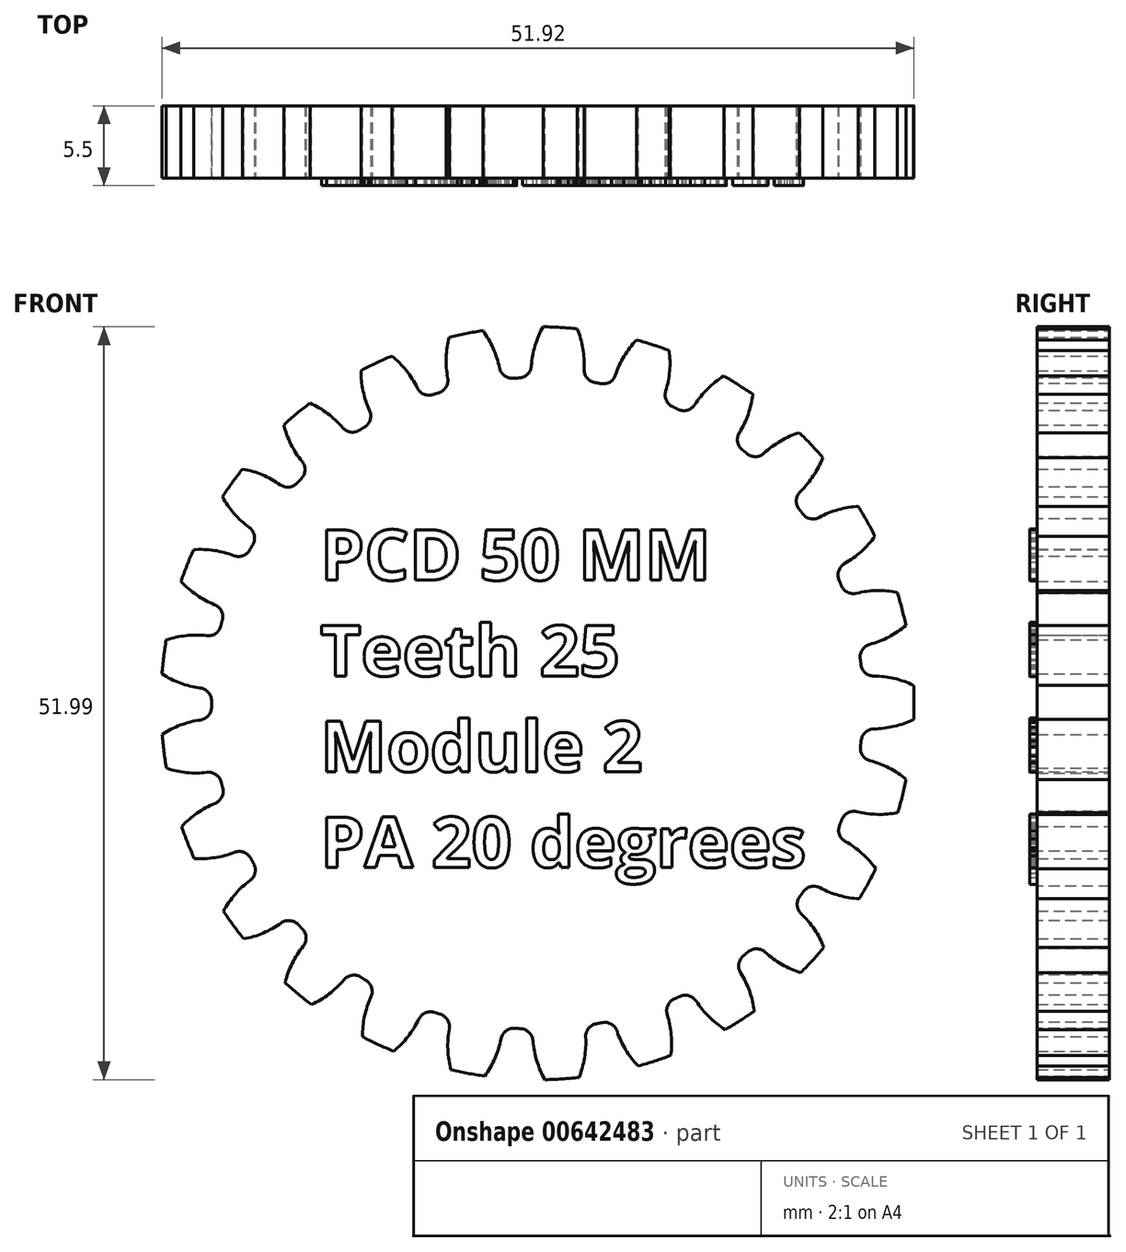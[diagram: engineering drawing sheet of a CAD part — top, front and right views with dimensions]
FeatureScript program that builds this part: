
annotation { "Feature Type Name" : "Feature", "Feature Type Description" : "" }
export const myFeature = defineFeature(function(context is Context, id is Id, definition is map)
    precondition{}
    {
        {
            var Q0;
            Q0=qCreatedBy(makeId("Front.planeOp"),FACE);
            var sketch = newSketch(context, id + "F0", { "sketchPlane" : qUnion([Q0])});
            skCircle(sketch, "E0", {"center": v(0, 0) * mm, "radius": 25 * mm, "construction": true});
            skLineSegment(sketch, "E1", {"start": v(0, 0) * mm, "end": v(0, 29.13) * mm, "construction": true});
            skLineSegment(sketch, "E2", {"start": v(0, 25) * mm, "end": v(44.14, 25) * mm, "construction": true});
            skLineSegment(sketch, "E3", {"start": v(0, 25) * mm, "end": v(44.14, 8.94) * mm});
            skLineSegment(sketch, "E4", {"start": v(0, 0) * mm, "end": v(8.03, 22.08) * mm, "construction": true});
            skCircle(sketch, "E5", {"center": v(0, 0) * mm, "radius": 23.5 * mm, "construction": true});
            skPoint(sketch, "E6", {"position": v(0, 26) * mm});
            skPoint(sketch, "E7", {"position": v(0, 23.5) * mm});
            skPoint(sketch, "E8", {"position": v(0, 25.16) * mm});
            skLineSegment(sketch, "E9", {"start": v(0, 25.16) * mm, "end": v(8.03, 22.08) * mm, "construction": true});
            skPoint(sketch, "E10", {"position": v(6.03, 22.85) * mm});
            skArc(sketch, "E11", {"start": v(0.4, 26) * mm, "mid": v(-0.26, 24.3) * mm, "end": v(-0.42, 22.5) * mm});
            skArc(sketch, "E12", {"start": v(-0.42, 22.5) * mm, "mid": v(12.32, 21.4) * mm, "end": v(0.4, 26) * mm, "construction": true});
            skPoint(sketch, "E13", {"position": v(-0.06, 25) * mm});
            skPoint(sketch, "E14", {"position": v(1.51, 24.95) * mm});
            skLineSegment(sketch, "E15", {"start": v(0, 0) * mm, "end": v(1.51, 24.95) * mm, "construction": true});
            skArc(sketch, "E16.MirrorCS", {"start": v(2.75, 25.85) * mm, "mid": v(3.2, 24.1) * mm, "end": v(3.13, 22.28) * mm});
            skArc(sketch, "E17", {"start": v(2.75, 25.85) * mm, "mid": v(1.57, 25.95) * mm, "end": v(0.4, 26) * mm});
            skArc(sketch, "E18", {"start": v(0.4, 26) * mm, "mid": v(-1.57, -25.95) * mm, "end": v(2.75, 25.85) * mm, "construction": true});
            skArc(sketch, "E19", {"start": v(-0.42, 22.5) * mm, "mid": v(-1.36, -22.46) * mm, "end": v(3.13, 22.28) * mm});
            skArc(sketch, "E20", {"start": v(3.13, 22.28) * mm, "mid": v(1.36, 22.46) * mm, "end": v(-0.42, 22.5) * mm, "construction": true});
            skSolve(sketch);
        }
        {
            var Q0;
            Q0=makeQuery(id+"F0.imprint","IMPRINT",FACE,{"disambiguationData":[TD([[makeQuery(id+"F0.imprint","IMPRINT",EDGE,{"derivedFrom":sQuery(id+"F0.wireOp",EDGE,"E11")}),1.0]])]});
            extrude(context, id + "F1", {"entities" : qUnion([Q0]), "depth" : 5 * mm, "offsetDistance" : 25 * mm});
        }
        {
            var Q0;
            Q0=makeQuery(id+"F1.opExtrude","SWEPT_EDGE",EDGE,{"disambiguationData":[OSD([sQuery(id+"F0.wireOp",EDGE,"E11"),sQuery(id+"F0.wireOp",EDGE,"E19")])]});
            var Q1;
            Q1=makeQuery(id+"F1.opExtrude","SWEPT_EDGE",EDGE,{"disambiguationData":[OSD([sQuery(id+"F0.wireOp",EDGE,"E16.MirrorCS"),sQuery(id+"F0.wireOp",EDGE,"E19")])]});
            fillet(context, id + "F2", {"entities" : qUnion([Q0, Q1]), "radius" : 0.9 * mm, "tangentPropagation" : true, "allowEdgeOverflow" : false});
        }
        {
            var Q0;
            Q0=makeQuery(id+"F1.opExtrude","SWEPT_BODY",BODY,{"disambiguationData":[OSD([sQuery(id+"F0.wireOp",EDGE,"E11"),sQuery(id+"F0.wireOp",EDGE,"E16.MirrorCS"),sQuery(id+"F0.wireOp",EDGE,"E17"),sQuery(id+"F0.wireOp",EDGE,"E19")])]});
            var Q1;
            Q1=makeQuery(id+"F1.opExtrude","SWEPT_FACE",FACE,{"disambiguationData":[OSD([sQuery(id+"F0.wireOp",EDGE,"E19")])]});
            circularPattern(context, id + "F3", {"operationType" : NewBodyOperationType.ADD, "entities" : qUnion([Q0]), "axis" : qUnion([Q1]), "angle" : 360 * degree, "instanceCount" : 25, "equalSpace" : true});
        }
        {
            var Q0;
            {var subQ0=makeQuery(id+"F1.opExtrude","CAP_FACE",FACE,{"disambiguationData":[OSD([sQuery(id+"F0.wireOp",EDGE,"E11"),sQuery(id+"F0.wireOp",EDGE,"E16.MirrorCS"),sQuery(id+"F0.wireOp",EDGE,"E17"),sQuery(id+"F0.wireOp",EDGE,"E19")])],"isStart":false});Q0=makeQuery(id+"F3.boolean.opBoolean","MERGE",FACE,{"derivedFrom":[subQ0,makeQuery(id+"F3.opPattern","COPY",FACE,{"derivedFrom":subQ0,"instanceName":"1"}),makeQuery(id+"F3.opPattern","COPY",FACE,{"derivedFrom":subQ0,"instanceName":"2"}),makeQuery(id+"F3.opPattern","COPY",FACE,{"derivedFrom":subQ0,"instanceName":"3"}),makeQuery(id+"F3.opPattern","COPY",FACE,{"derivedFrom":subQ0,"instanceName":"4"}),makeQuery(id+"F3.opPattern","COPY",FACE,{"derivedFrom":subQ0,"instanceName":"5"}),makeQuery(id+"F3.opPattern","COPY",FACE,{"derivedFrom":subQ0,"instanceName":"6"}),makeQuery(id+"F3.opPattern","COPY",FACE,{"derivedFrom":subQ0,"instanceName":"7"}),makeQuery(id+"F3.opPattern","COPY",FACE,{"derivedFrom":subQ0,"instanceName":"8"}),makeQuery(id+"F3.opPattern","COPY",FACE,{"derivedFrom":subQ0,"instanceName":"9"}),makeQuery(id+"F3.opPattern","COPY",FACE,{"derivedFrom":subQ0,"instanceName":"10"}),makeQuery(id+"F3.opPattern","COPY",FACE,{"derivedFrom":subQ0,"instanceName":"11"}),makeQuery(id+"F3.opPattern","COPY",FACE,{"derivedFrom":subQ0,"instanceName":"12"}),makeQuery(id+"F3.opPattern","COPY",FACE,{"derivedFrom":subQ0,"instanceName":"13"}),makeQuery(id+"F3.opPattern","COPY",FACE,{"derivedFrom":subQ0,"instanceName":"14"}),makeQuery(id+"F3.opPattern","COPY",FACE,{"derivedFrom":subQ0,"instanceName":"15"}),makeQuery(id+"F3.opPattern","COPY",FACE,{"derivedFrom":subQ0,"instanceName":"16"}),makeQuery(id+"F3.opPattern","COPY",FACE,{"derivedFrom":subQ0,"instanceName":"17"}),makeQuery(id+"F3.opPattern","COPY",FACE,{"derivedFrom":subQ0,"instanceName":"18"}),makeQuery(id+"F3.opPattern","COPY",FACE,{"derivedFrom":subQ0,"instanceName":"19"}),makeQuery(id+"F3.opPattern","COPY",FACE,{"derivedFrom":subQ0,"instanceName":"20"}),makeQuery(id+"F3.opPattern","COPY",FACE,{"derivedFrom":subQ0,"instanceName":"21"}),makeQuery(id+"F3.opPattern","COPY",FACE,{"derivedFrom":subQ0,"instanceName":"22"}),makeQuery(id+"F3.opPattern","COPY",FACE,{"derivedFrom":subQ0,"instanceName":"23"}),makeQuery(id+"F3.opPattern","COPY",FACE,{"derivedFrom":subQ0,"instanceName":"24"})]});}
            var sketch = newSketch(context, id + "F4", { "sketchPlane" : qUnion([Q0])});
            skText(sketch, "E21", { "text": "PCD 50 MM\nTeeth 25\nModule 2\nPA 20 degrees ", "fontName": "OpenSans-Bold.ttf"});
            const initialGuessF4  = {"E21": [-0.015, 0.0085, 1, 0, 0.0035]};
            skSetInitialGuess(sketch, initialGuessF4);
            skSolve(sketch);
        }
        {
            var Q0;
            Q0 = qSketchRegion(id + "F4", true);
            extrude(context, id + "F5", {"entities" : qUnion([Q0]), "operationType" : NewBodyOperationType.ADD, "depth" : 0.5 * mm, "offsetDistance" : 25 * mm});
        }
    });
